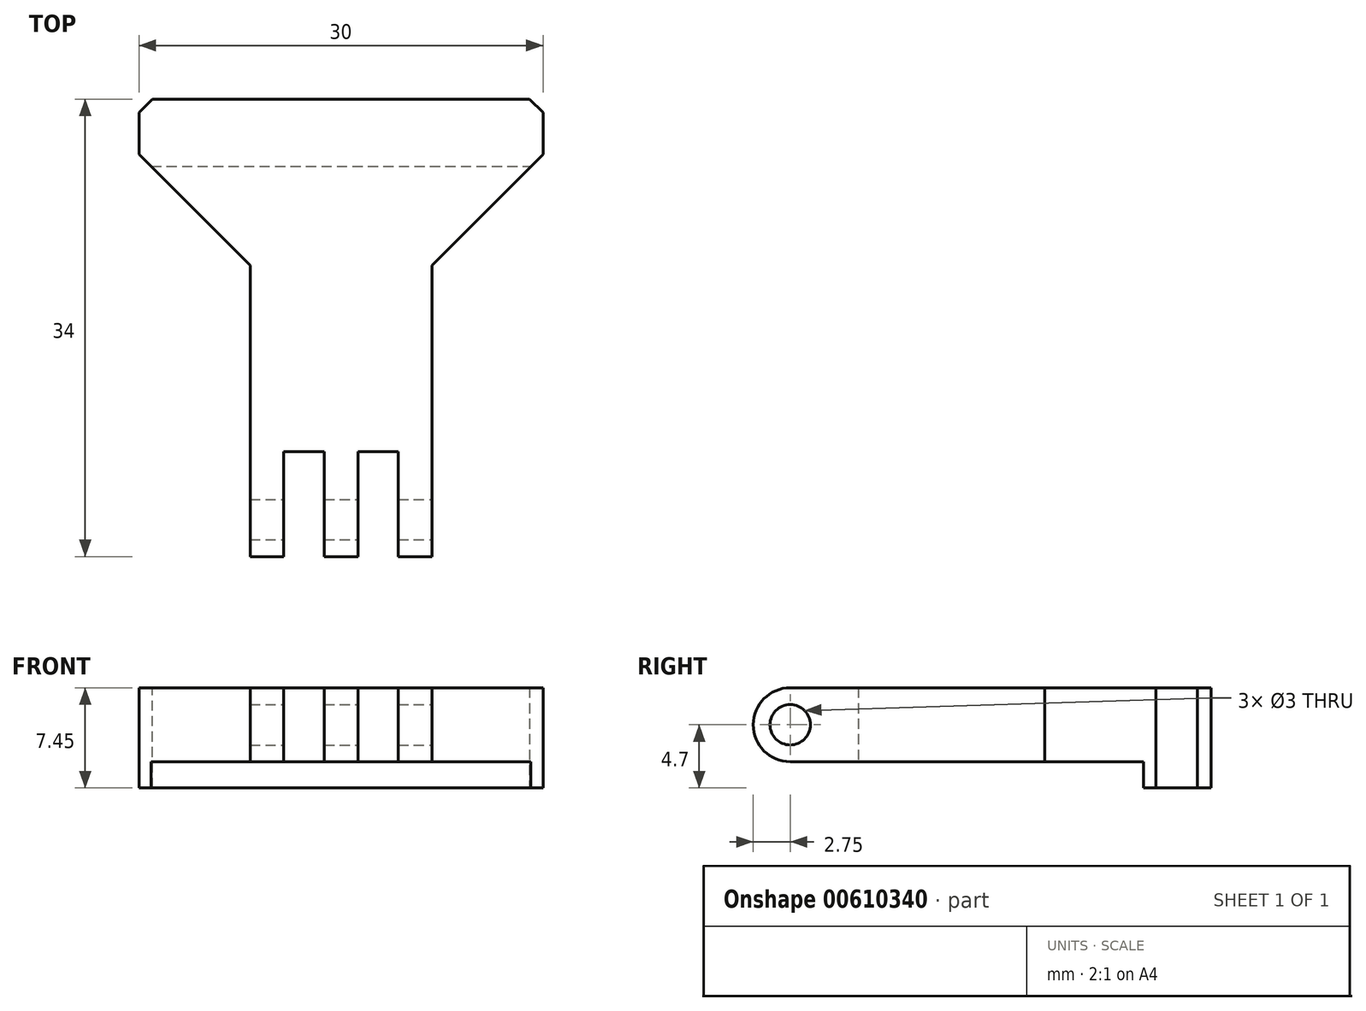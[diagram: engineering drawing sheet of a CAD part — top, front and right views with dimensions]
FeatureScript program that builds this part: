
annotation { "Feature Type Name" : "Feature", "Feature Type Description" : "" }
export const myFeature = defineFeature(function(context is Context, id is Id, definition is map)
    precondition{}
    {
        {
            var Q0;
            Q0=qCreatedBy(makeId("Top.planeOp"),FACE);
            var sketch = newSketch(context, id + "F0", { "sketchPlane" : qUnion([Q0])});
            skLineSegment(sketch, "E0", {"start": v(-15, 12) * mm, "end": v(-15, 17) * mm});
            skLineSegment(sketch, "E1", {"start": v(-15, 17) * mm, "end": v(15, 17) * mm});
            skLineSegment(sketch, "E2", {"start": v(15, 17) * mm, "end": v(15, 12) * mm});
            skLineSegment(sketch, "E3", {"start": v(6.75, -17) * mm, "end": v(6.75, 4.65) * mm});
            skLineSegment(sketch, "E4", {"start": v(-6.75, -17) * mm, "end": v(-6.75, 4.65) * mm});
            skLineSegment(sketch, "E5", {"start": v(-15, 12) * mm, "end": v(-15, 4.65) * mm});
            skLineSegment(sketch, "E6", {"start": v(-15, 4.65) * mm, "end": v(-6.75, 4.65) * mm});
            skLineSegment(sketch, "E7", {"start": v(15, 12) * mm, "end": v(15, 4.65) * mm});
            skLineSegment(sketch, "E8", {"start": v(15, 4.65) * mm, "end": v(6.75, 4.65) * mm});
            skLineSegment(sketch, "E9", {"start": v(-6.75, -17) * mm, "end": v(-4.25, -17) * mm});
            skLineSegment(sketch, "E10", {"start": v(-4.25, -17) * mm, "end": v(-4.25, -9.2) * mm});
            skLineSegment(sketch, "E11", {"start": v(-4.25, -9.2) * mm, "end": v(-1.25, -9.2) * mm});
            skLineSegment(sketch, "E12", {"start": v(-1.25, -9.2) * mm, "end": v(-1.25, -17) * mm});
            skLineSegment(sketch, "E13", {"start": v(-1.25, -17) * mm, "end": v(1.25, -17) * mm});
            skLineSegment(sketch, "E14", {"start": v(1.25, -17) * mm, "end": v(1.25, -9.2) * mm});
            skLineSegment(sketch, "E15", {"start": v(1.25, -9.2) * mm, "end": v(4.25, -9.2) * mm});
            skLineSegment(sketch, "E16", {"start": v(4.25, -9.2) * mm, "end": v(4.25, -17) * mm});
            skLineSegment(sketch, "E17", {"start": v(4.25, -17) * mm, "end": v(6.75, -17) * mm});
            skSolve(sketch);
        }
        {
            var Q0;
            Q0=makeQuery(id+"F0.imprint","IMPRINT",FACE,{"disambiguationData":[TD([[makeQuery(id+"F0.imprint","IMPRINT",EDGE,{"derivedFrom":sQuery(id+"F0.wireOp",EDGE,"E0")}),-1.0]])]});
            extrude(context, id + "F1", {"entities" : qUnion([Q0]), "endBound" : BoundingType.SYMMETRIC, "depth" : 5.5 * mm, "offsetDistance" : 25 * mm});
        }
        {
            var Q0;
            Q0=makeQuery(id+"F1.opExtrude","CAP_FACE",FACE,{"disambiguationData":[OSD([sQuery(id+"F0.wireOp",EDGE,"E0"),sQuery(id+"F0.wireOp",EDGE,"E1"),sQuery(id+"F0.wireOp",EDGE,"E2"),sQuery(id+"F0.wireOp",EDGE,"7c8aT4zF-lR4I-qTAC-FfzC-Epl1jPGJCpL0"),sQuery(id+"F0.wireOp",EDGE,"4eEl08Rx-sWw6-f9pj-CJ1Y-upnnrAsZboQy"),sQuery(id+"F0.wireOp",EDGE,"E3"),sQuery(id+"F0.wireOp",EDGE,"CwxFINe9-NNDO-eMLE-aiot-7BejCXbgUlda"),sQuery(id+"F0.wireOp",EDGE,"E4"),sQuery(id+"F0.wireOp",EDGE,"FZ8XlSSW-A1rL-0F4U-VaLa-jAqCqLE27K7x")])],"isStart":true});
            var sketch = newSketch(context, id + "F2", { "sketchPlane" : qUnion([Q0])});
            skLineSegment(sketch, "E18", {"start": v(-15, -17) * mm, "end": v(-15, -12) * mm});
            skLineSegment(sketch, "E19", {"start": v(15, -17) * mm, "end": v(15, -17) * mm});
            skLineSegment(sketch, "E20", {"start": v(15, -17) * mm, "end": v(-15, -17) * mm});
            skLineSegment(sketch, "E21", {"start": v(-15, -12) * mm, "end": v(15, -12) * mm});
            skLineSegment(sketch, "E22", {"start": v(15, -12) * mm, "end": v(15, -17) * mm});
            skSolve(sketch);
        }
        {
            var Q0;
            Q0=makeQuery(id+"F2.imprint","IMPRINT",FACE,{"disambiguationData":[TD([[makeQuery(id+"F2.imprint","IMPRINT",EDGE,{"derivedFrom":sQuery(id+"F2.wireOp",EDGE,"E18")}),1.0]])]});
            extrude(context, id + "F3", {"entities" : qUnion([Q0]), "operationType" : NewBodyOperationType.ADD, "depth" : 1.95 * mm, "offsetDistance" : 25 * mm});
        }
        {
            var Q0;
            Q0=makeQuery(id+"F1.opExtrude","SWEPT_EDGE",EDGE,{"disambiguationData":[OSD([sQuery(id+"F0.wireOp",EDGE,"E5"),sQuery(id+"F0.wireOp",EDGE,"E6")])]});
            var Q1;
            Q1=makeQuery(id+"F1.opExtrude","SWEPT_EDGE",EDGE,{"disambiguationData":[OSD([sQuery(id+"F0.wireOp",EDGE,"E7"),sQuery(id+"F0.wireOp",EDGE,"E8")])]});
            chamfer(context, id + "F4", {"entities" : qUnion([Q0, Q1]), "width" : 8.25 * mm, "tangentPropagation" : true});
        }
        {
            var Q0;
            Q0=makeQuery(id+"F3.boolean.opBoolean","MERGE",EDGE,{"derivedFrom":[makeQuery(id+"F1.opExtrude","SWEPT_EDGE",EDGE,{"disambiguationData":[OSD([sQuery(id+"F0.wireOp",EDGE,"E1"),sQuery(id+"F0.wireOp",EDGE,"E2")])]}),makeQuery(id+"F3.opExtrude","SWEPT_EDGE",EDGE,{"disambiguationData":[OSD([sQuery(id+"F2.wireOp",EDGE,"E20"),sQuery(id+"F2.wireOp",EDGE,"E22")])]})]});
            var Q1;
            Q1=makeQuery(id+"F3.boolean.opBoolean","MERGE",EDGE,{"derivedFrom":[makeQuery(id+"F1.opExtrude","SWEPT_EDGE",EDGE,{"disambiguationData":[OSD([sQuery(id+"F0.wireOp",EDGE,"E0"),sQuery(id+"F0.wireOp",EDGE,"E1")])]}),makeQuery(id+"F3.opExtrude","SWEPT_EDGE",EDGE,{"disambiguationData":[OSD([sQuery(id+"F2.wireOp",EDGE,"E18"),sQuery(id+"F2.wireOp",EDGE,"E20")])]})]});
            chamfer(context, id + "F5", {"entities" : qUnion([Q0, Q1]), "width" : 1 * mm, "tangentPropagation" : true});
        }
        {
            var Q0;
            Q0=makeQuery(id+"F1.opExtrude","CAP_EDGE",EDGE,{"disambiguationData":[OSD([sQuery(id+"F0.wireOp",EDGE,"E17")])],"isStart":false});
            var Q1;
            Q1=makeQuery(id+"F1.opExtrude","CAP_EDGE",EDGE,{"disambiguationData":[OSD([sQuery(id+"F0.wireOp",EDGE,"E13")])],"isStart":false});
            var Q2;
            Q2=makeQuery(id+"F1.opExtrude","CAP_EDGE",EDGE,{"disambiguationData":[OSD([sQuery(id+"F0.wireOp",EDGE,"E9")])],"isStart":false});
            var Q3;
            Q3=makeQuery(id+"F1.opExtrude","CAP_EDGE",EDGE,{"disambiguationData":[OSD([sQuery(id+"F0.wireOp",EDGE,"E17")])],"isStart":true});
            var Q4;
            Q4=makeQuery(id+"F1.opExtrude","CAP_EDGE",EDGE,{"disambiguationData":[OSD([sQuery(id+"F0.wireOp",EDGE,"E13")])],"isStart":true});
            var Q5;
            Q5=makeQuery(id+"F1.opExtrude","CAP_EDGE",EDGE,{"disambiguationData":[OSD([sQuery(id+"F0.wireOp",EDGE,"E9")])],"isStart":true});
            fillet(context, id + "F6", {"entities" : qUnion([Q0, Q1, Q2, Q3, Q4, Q5]), "radius" : 2.75 * mm, "tangentPropagation" : true, "allowEdgeOverflow" : false});
        }
        {
            var Q0;
            Q0=makeQuery(id+"F1.opExtrude","SWEPT_FACE",FACE,{"disambiguationData":[OSD([sQuery(id+"F0.wireOp",EDGE,"E3")])]});
            var sketch = newSketch(context, id + "F7", { "sketchPlane" : qUnion([Q0])});
            skPoint(sketch, "E23", {"position": v(-14.25, 0) * mm});
            skSolve(sketch);
        }
        {
            var Q0;
            Q0=sQuery(id+"F7.wireOp",VERTEX,"E23");
            var Q1;
            Q1=makeQuery(id+"F1.opExtrude","SWEPT_BODY",BODY,{"disambiguationData":[OSD([sQuery(id+"F0.wireOp",EDGE,"E0"),sQuery(id+"F0.wireOp",EDGE,"E1"),sQuery(id+"F0.wireOp",EDGE,"E2"),sQuery(id+"F0.wireOp",EDGE,"E3"),sQuery(id+"F0.wireOp",EDGE,"E4"),sQuery(id+"F0.wireOp",EDGE,"E5"),sQuery(id+"F0.wireOp",EDGE,"E6"),sQuery(id+"F0.wireOp",EDGE,"E7"),sQuery(id+"F0.wireOp",EDGE,"E8"),sQuery(id+"F0.wireOp",EDGE,"E9"),sQuery(id+"F0.wireOp",EDGE,"E10"),sQuery(id+"F0.wireOp",EDGE,"E11"),sQuery(id+"F0.wireOp",EDGE,"E12"),sQuery(id+"F0.wireOp",EDGE,"E13"),sQuery(id+"F0.wireOp",EDGE,"E14"),sQuery(id+"F0.wireOp",EDGE,"E15"),sQuery(id+"F0.wireOp",EDGE,"E16"),sQuery(id+"F0.wireOp",EDGE,"E17")])]});
            hole(context, id + "F8", {"style" : HoleStyle.SIMPLE, "endStyle" : HoleEndStyle.THROUGH, "holeDiameter" : 3 * mm, "majorDiameter" : 5 * mm, "isTappedThrough" : true, "tappedDepth" : 2.9 * mm, "tapClearance" : 3, "startFromSketch" : true, "locations" : qUnion([Q0]), "scope" : qUnion([Q1])});
        }
    });
